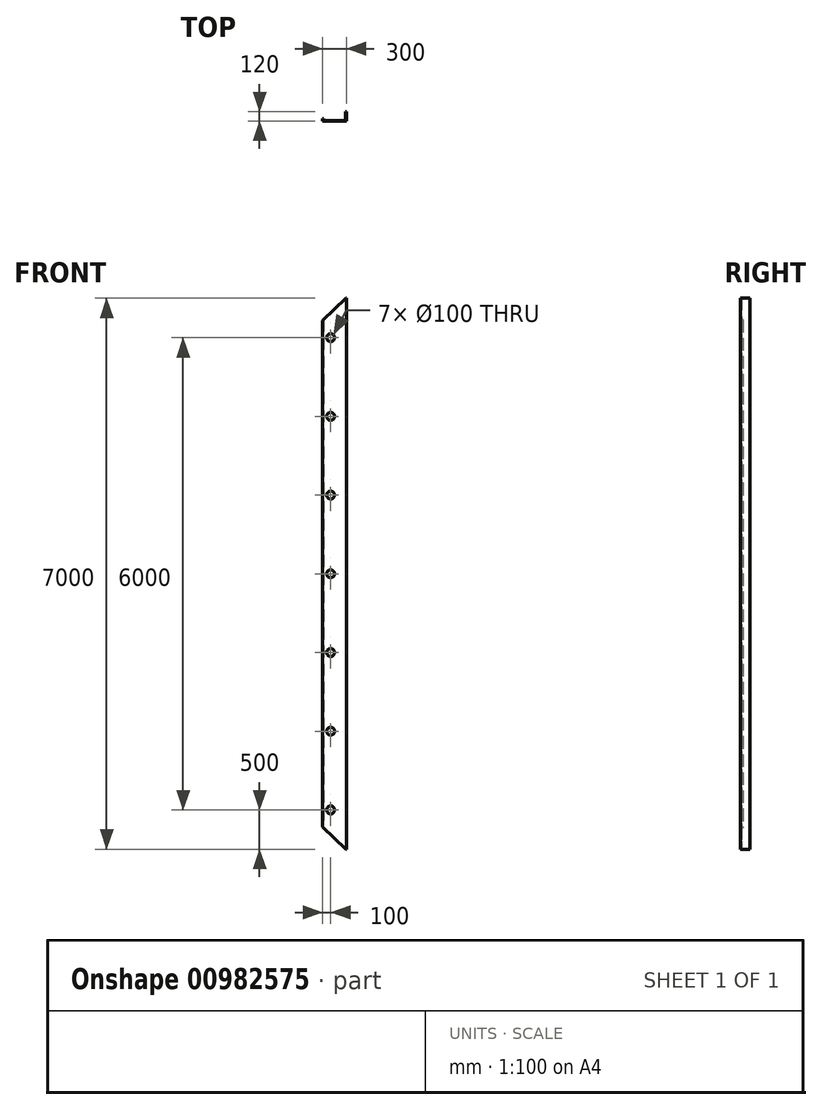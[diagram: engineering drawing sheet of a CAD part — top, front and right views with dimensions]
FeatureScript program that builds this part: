
annotation { "Feature Type Name" : "Feature", "Feature Type Description" : "" }
export const myFeature = defineFeature(function(context is Context, id is Id, definition is map)
    precondition{}
    {
        {
            var Q0;
            Q0=qCreatedBy(makeId("Top.planeOp"),FACE);
            var sketch = newSketch(context, id + "F0", { "sketchPlane" : qUnion([Q0])});
            skLineSegment(sketch, "E0", {"start": v(-110, 0) * mm, "end": v(-100, 0) * mm});
            skLineSegment(sketch, "E1", {"start": v(-100, 0) * mm, "end": v(-100, -20) * mm});
            skLineSegment(sketch, "E2", {"start": v(-100, -20) * mm, "end": v(180, -20) * mm});
            skLineSegment(sketch, "E3", {"start": v(180, -20) * mm, "end": v(180, 90) * mm});
            skLineSegment(sketch, "E4", {"start": v(180, 90) * mm, "end": v(190, 90) * mm});
            skLineSegment(sketch, "E5", {"start": v(190, 90) * mm, "end": v(190, -30) * mm});
            skLineSegment(sketch, "E6", {"start": v(190, -30) * mm, "end": v(-110, -30) * mm});
            skLineSegment(sketch, "E7", {"start": v(-110, -30) * mm, "end": v(-110, 0) * mm});
            skSolve(sketch);
        }
        {
            var Q0;
            Q0 = qSketchRegion(id + "F0", true);
            extrude(context, id + "F1", {"entities" : qUnion([Q0]), "depth" : 7000 * mm, "offsetDistance" : 25 * mm});
        }
        {
            var Q0;
            Q0=makeQuery(id+"F1.opExtrude","SWEPT_FACE",FACE,{"disambiguationData":[OSD([sQuery(id+"F0.wireOp",EDGE,"E6")])]});
            var sketch = newSketch(context, id + "F2", { "sketchPlane" : qUnion([Q0])});
            skLineSegment(sketch, "E8", {"start": v(-310, 6524.02) * mm, "end": v(-310, 7200) * mm});
            skLineSegment(sketch, "E9", {"start": v(-310, 7200) * mm, "end": v(390, 7200) * mm});
            skLineSegment(sketch, "E10", {"start": v(390, 7200) * mm, "end": v(-310, 6524.02) * mm});
            skLineSegment(sketch, "E11", {"start": v(-2423.37, 3500) * mm, "end": v(3096.96, 3500) * mm});
            skLineSegment(sketch, "E12.MirrorCS", {"start": v(-310, -200) * mm, "end": v(390, -200) * mm});
            skLineSegment(sketch, "E13.MirrorCS", {"start": v(-310, 475.98) * mm, "end": v(-310, -200) * mm});
            skLineSegment(sketch, "E14.MirrorCS", {"start": v(390, -200) * mm, "end": v(-310, 475.98) * mm});
            skSolve(sketch);
        }
        {
            var Q0;
            {var subQ0=sQuery(id+"F2.wireOp",EDGE,"E14.MirrorCS");var subQ1=sQuery(id+"F0.wireOp",EDGE,"E6");var subQ2=makeQuery(id+"F1.opExtrude","CAP_EDGE",EDGE,{"disambiguationData":[OSD([subQ1])],"isStart":true});var subQ3=makeQuery(id+"F2.imprint","INTERSECT",VERTEX,{"derivedFrom":[subQ2,subQ0]});Q0=makeQuery(id+"F2.imprint","IMPRINT",FACE,{"disambiguationData":[TD([[makeQuery(id+"F2.imprint","IMPRINT",EDGE,{"disambiguationData":[TD([[subQ3,-1.0]])],"derivedFrom":subQ0}),1.0]])]});}
            var Q1;
            {var subQ0=sQuery(id+"F2.wireOp",EDGE,"E10");var subQ1=sQuery(id+"F0.wireOp",EDGE,"E6");var subQ2=makeQuery(id+"F1.opExtrude","CAP_EDGE",EDGE,{"disambiguationData":[OSD([subQ1])],"isStart":false});var subQ3=makeQuery(id+"F2.imprint","INTERSECT",VERTEX,{"derivedFrom":[subQ2,subQ0]});Q1=makeQuery(id+"F2.imprint","IMPRINT",FACE,{"disambiguationData":[TD([[makeQuery(id+"F2.imprint","IMPRINT",EDGE,{"disambiguationData":[TD([[subQ3,-1.0]])],"derivedFrom":subQ0}),-1.0]])]});}
            extrude(context, id + "F3", {"entities" : qUnion([Q0, Q1]), "operationType" : NewBodyOperationType.REMOVE, "oppositeDirection" : true, "depth" : 200 * mm, "offsetDistance" : 25 * mm});
        }
        {
            var Q0;
            Q0=makeQuery(id+"F1.opExtrude","SWEPT_FACE",FACE,{"disambiguationData":[OSD([sQuery(id+"F0.wireOp",EDGE,"E6")])]});
            var sketch = newSketch(context, id + "F4", { "sketchPlane" : qUnion([Q0])});
            skCircle(sketch, "E15", {"center": v(-10, 6500) * mm, "radius": 50 * mm});
            skCircle(sketch, "E16.0.1.0", {"center": v(-10, 5500) * mm, "radius": 50 * mm});
            skCircle(sketch, "E16.0.2.0", {"center": v(-10, 4500) * mm, "radius": 50 * mm});
            skCircle(sketch, "E16.0.3.0", {"center": v(-10, 3500) * mm, "radius": 50 * mm});
            skCircle(sketch, "E16.0.4.0", {"center": v(-10, 2500) * mm, "radius": 50 * mm});
            skCircle(sketch, "E16.0.5.0", {"center": v(-10, 1500) * mm, "radius": 50 * mm});
            skCircle(sketch, "E16.0.6.0", {"center": v(-10, 500) * mm, "radius": 50 * mm});
            skLineSegment(sketch, "E16.direction1", {"start": v(-10, 6650) * mm, "end": v(15, 6650) * mm, "construction": true});
            skLineSegment(sketch, "E16.direction2", {"start": v(-10, 6650) * mm, "end": v(-10, 5650) * mm, "construction": true});
            skSolve(sketch);
        }
        {
            var Q0;
            Q0=makeQuery(id+"F4.imprint","IMPRINT",FACE,{"disambiguationData":[TD([[makeQuery(id+"F4.imprint","IMPRINT",EDGE,{"derivedFrom":sQuery(id+"F4.wireOp",EDGE,"E15")}),1.0]])]});
            var Q1;
            Q1=makeQuery(id+"F4.imprint","IMPRINT",FACE,{"disambiguationData":[TD([[makeQuery(id+"F4.imprint","IMPRINT",EDGE,{"derivedFrom":sQuery(id+"F4.wireOp",EDGE,"E16.0.1.0")}),1.0]])]});
            var Q2;
            Q2=makeQuery(id+"F4.imprint","IMPRINT",FACE,{"disambiguationData":[TD([[makeQuery(id+"F4.imprint","IMPRINT",EDGE,{"derivedFrom":sQuery(id+"F4.wireOp",EDGE,"E16.0.2.0")}),1.0]])]});
            var Q3;
            Q3=makeQuery(id+"F4.imprint","IMPRINT",FACE,{"disambiguationData":[TD([[makeQuery(id+"F4.imprint","IMPRINT",EDGE,{"derivedFrom":sQuery(id+"F4.wireOp",EDGE,"E16.0.3.0")}),1.0]])]});
            var Q4;
            Q4=makeQuery(id+"F4.imprint","IMPRINT",FACE,{"disambiguationData":[TD([[makeQuery(id+"F4.imprint","IMPRINT",EDGE,{"derivedFrom":sQuery(id+"F4.wireOp",EDGE,"E16.0.4.0")}),1.0]])]});
            var Q5;
            Q5=makeQuery(id+"F4.imprint","IMPRINT",FACE,{"disambiguationData":[TD([[makeQuery(id+"F4.imprint","IMPRINT",EDGE,{"derivedFrom":sQuery(id+"F4.wireOp",EDGE,"E16.0.5.0")}),1.0]])]});
            var Q6;
            Q6=makeQuery(id+"F4.imprint","IMPRINT",FACE,{"disambiguationData":[TD([[makeQuery(id+"F4.imprint","IMPRINT",EDGE,{"derivedFrom":sQuery(id+"F4.wireOp",EDGE,"E16.0.6.0")}),1.0]])]});
            extrude(context, id + "F5", {"entities" : qUnion([Q0, Q1, Q2, Q3, Q4, Q5, Q6]), "operationType" : NewBodyOperationType.REMOVE, "endBound" : BoundingType.THROUGH_ALL, "oppositeDirection" : true, "depth" : 25 * mm, "offsetDistance" : 25 * mm});
        }
    });
